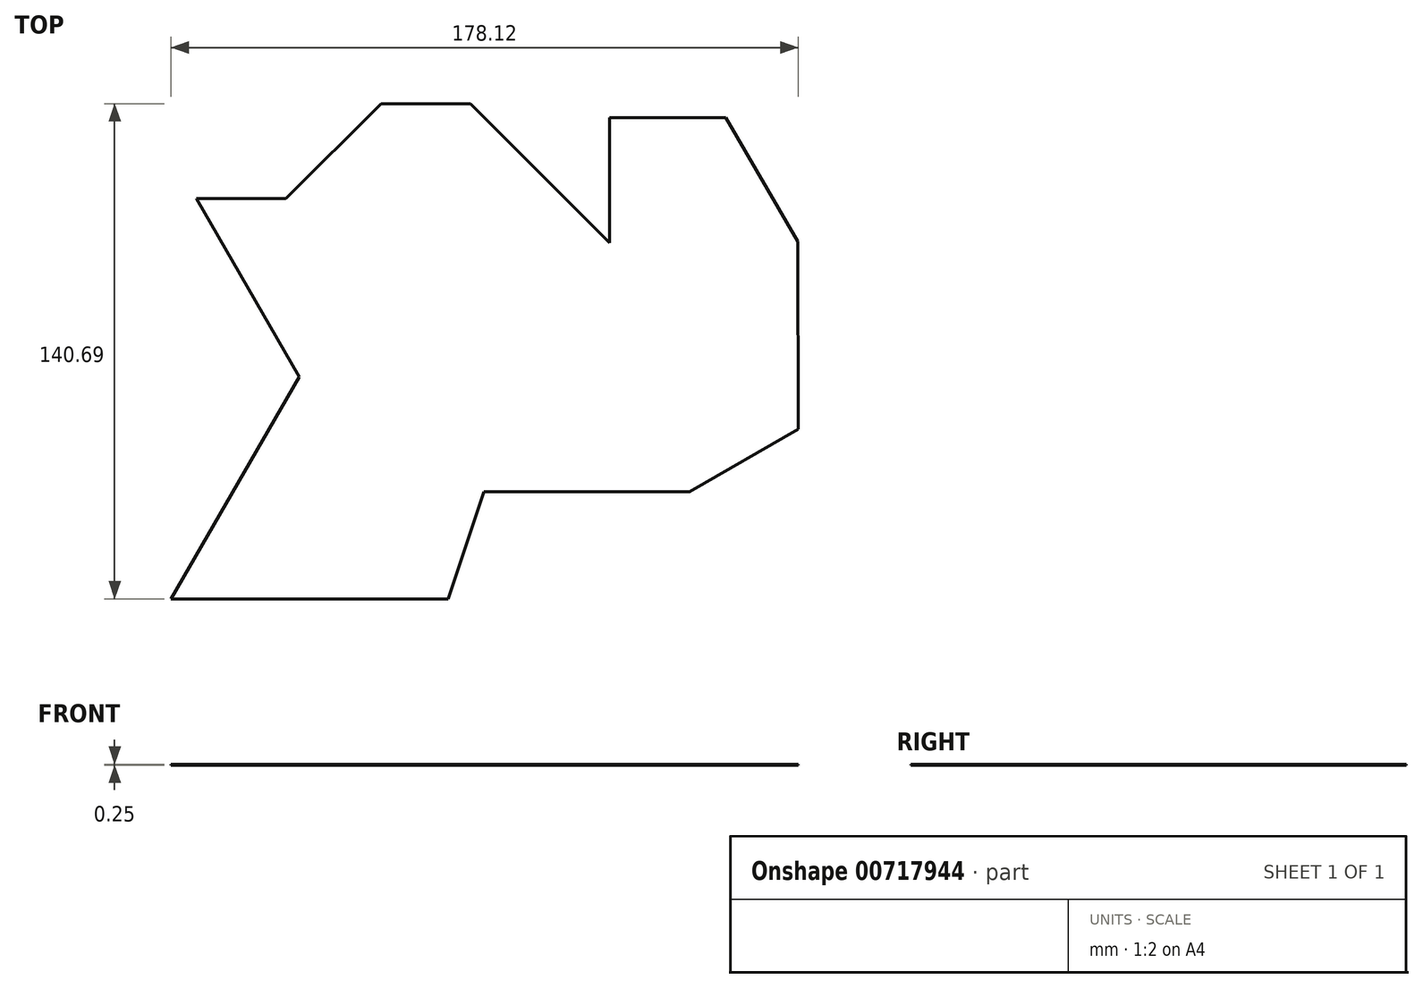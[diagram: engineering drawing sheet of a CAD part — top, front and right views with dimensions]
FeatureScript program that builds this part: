
annotation { "Feature Type Name" : "Feature", "Feature Type Description" : "" }
export const myFeature = defineFeature(function(context is Context, id is Id, definition is map)
    precondition{}
    {
        {
            var Q0;
            Q0=qCreatedBy(makeId("Top.planeOp"),FACE);
            var sketch = newSketch(context, id + "F0", { "sketchPlane" : qUnion([Q0])});
            skLineSegment(sketch, "E0", {"start": v(0, 0) * mm, "end": v(78.74, 0) * mm});
            skLineSegment(sketch, "E1", {"start": v(78.74, 0) * mm, "end": v(88.9, 30.48) * mm});
            skLineSegment(sketch, "E2", {"start": v(88.9, 30.48) * mm, "end": v(147.32, 30.48) * mm});
            skLineSegment(sketch, "E3", {"start": v(147.32, 30.48) * mm, "end": v(178.12, 48.26) * mm});
            skLineSegment(sketch, "E4", {"start": v(178.12, 48.26) * mm, "end": v(177.95, 101.6) * mm});
            skLineSegment(sketch, "E5", {"start": v(177.95, 101.6) * mm, "end": v(157.52, 136.73) * mm});
            skLineSegment(sketch, "E6", {"start": v(157.52, 136.73) * mm, "end": v(124.5, 136.73) * mm});
            skLineSegment(sketch, "E7", {"start": v(124.5, 136.73) * mm, "end": v(124.5, 101.17) * mm});
            skLineSegment(sketch, "E8", {"start": v(124.5, 101.17) * mm, "end": v(85, 140.69) * mm});
            skLineSegment(sketch, "E9", {"start": v(85, 140.69) * mm, "end": v(59.6, 140.69) * mm});
            skLineSegment(sketch, "E10", {"start": v(59.6, 140.69) * mm, "end": v(32.65, 113.74) * mm});
            skLineSegment(sketch, "E11", {"start": v(32.65, 113.74) * mm, "end": v(7.25, 113.74) * mm});
            skLineSegment(sketch, "E12", {"start": v(7.25, 113.74) * mm, "end": v(36.46, 63.15) * mm});
            skLineSegment(sketch, "E13", {"start": v(36.46, 63.15) * mm, "end": v(0, 0) * mm});
            skSolve(sketch);
        }
        {
            var Q0;
            Q0=makeQuery(id+"F0.imprint","IMPRINT",FACE,{"disambiguationData":[TD([[makeQuery(id+"F0.imprint","IMPRINT",EDGE,{"derivedFrom":sQuery(id+"F0.wireOp",EDGE,"E0")}),1.0]])]});
            extrude(context, id + "F1", {"entities" : qUnion([Q0]), "depth" : 0.25 * mm, "offsetDistance" : 25.4 * mm});
        }
    });
